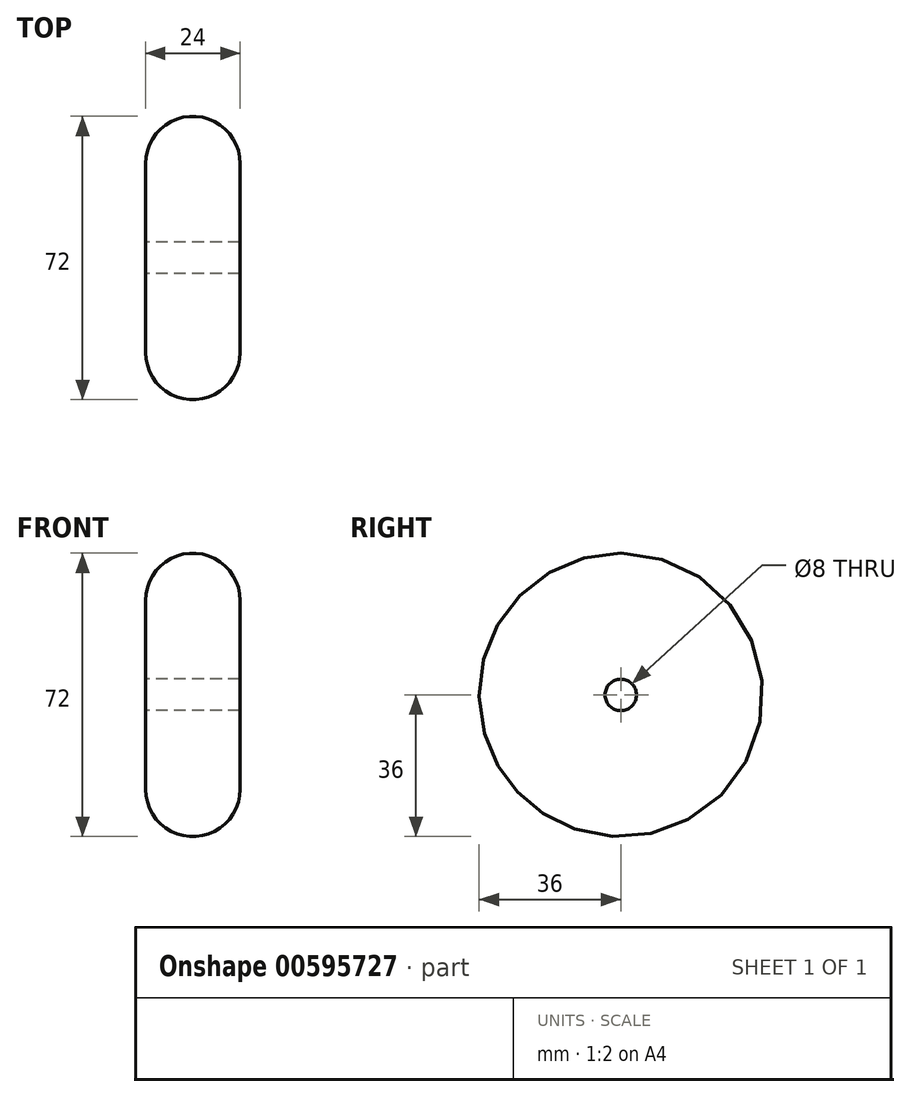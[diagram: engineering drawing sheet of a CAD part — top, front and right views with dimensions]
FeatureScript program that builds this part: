
annotation { "Feature Type Name" : "Feature", "Feature Type Description" : "" }
export const myFeature = defineFeature(function(context is Context, id is Id, definition is map)
    precondition{}
    {
        {
            var Q0;
            Q0=qCreatedBy(makeId("Front.planeOp"),FACE);
            var sketch = newSketch(context, id + "F0", { "sketchPlane" : qUnion([Q0])});
            skLineSegment(sketch, "E0.bottom", {"start": v(-12, 4) * mm, "end": v(12, 4) * mm});
            skLineSegment(sketch, "E0.left", {"start": v(-12, 4) * mm, "end": v(-12, 24) * mm});
            skLineSegment(sketch, "E0.right", {"start": v(12, 4) * mm, "end": v(12, 24) * mm});
            skPoint(sketch, "E0.middle", {"position": v(0, 14) * mm});
            skArc(sketch, "E1", {"start": v(-12, 24) * mm, "mid": v(0, 36) * mm, "end": v(12, 24) * mm});
            skPoint(sketch, "E2", {"position": v(0, 36) * mm});
            skLineSegment(sketch, "E3", {"start": v(-36.37, 0) * mm, "end": v(38.9, 0) * mm, "construction": true});
            skSolve(sketch);
        }
        {
            var Q0;
            Q0 = qSketchRegion(id + "F0", true);
            var Q1;
            Q1=sQuery(id+"F0.wireOp",EDGE,"E3");
            revolve(context, id + "F1", {"surfaceOperationType" : NewSurfaceOperationType.NEW, "entities" : qUnion([Q0]), "axis" : qUnion([Q1]), "revolveType" : RevolveType.FULL});
        }
    });
